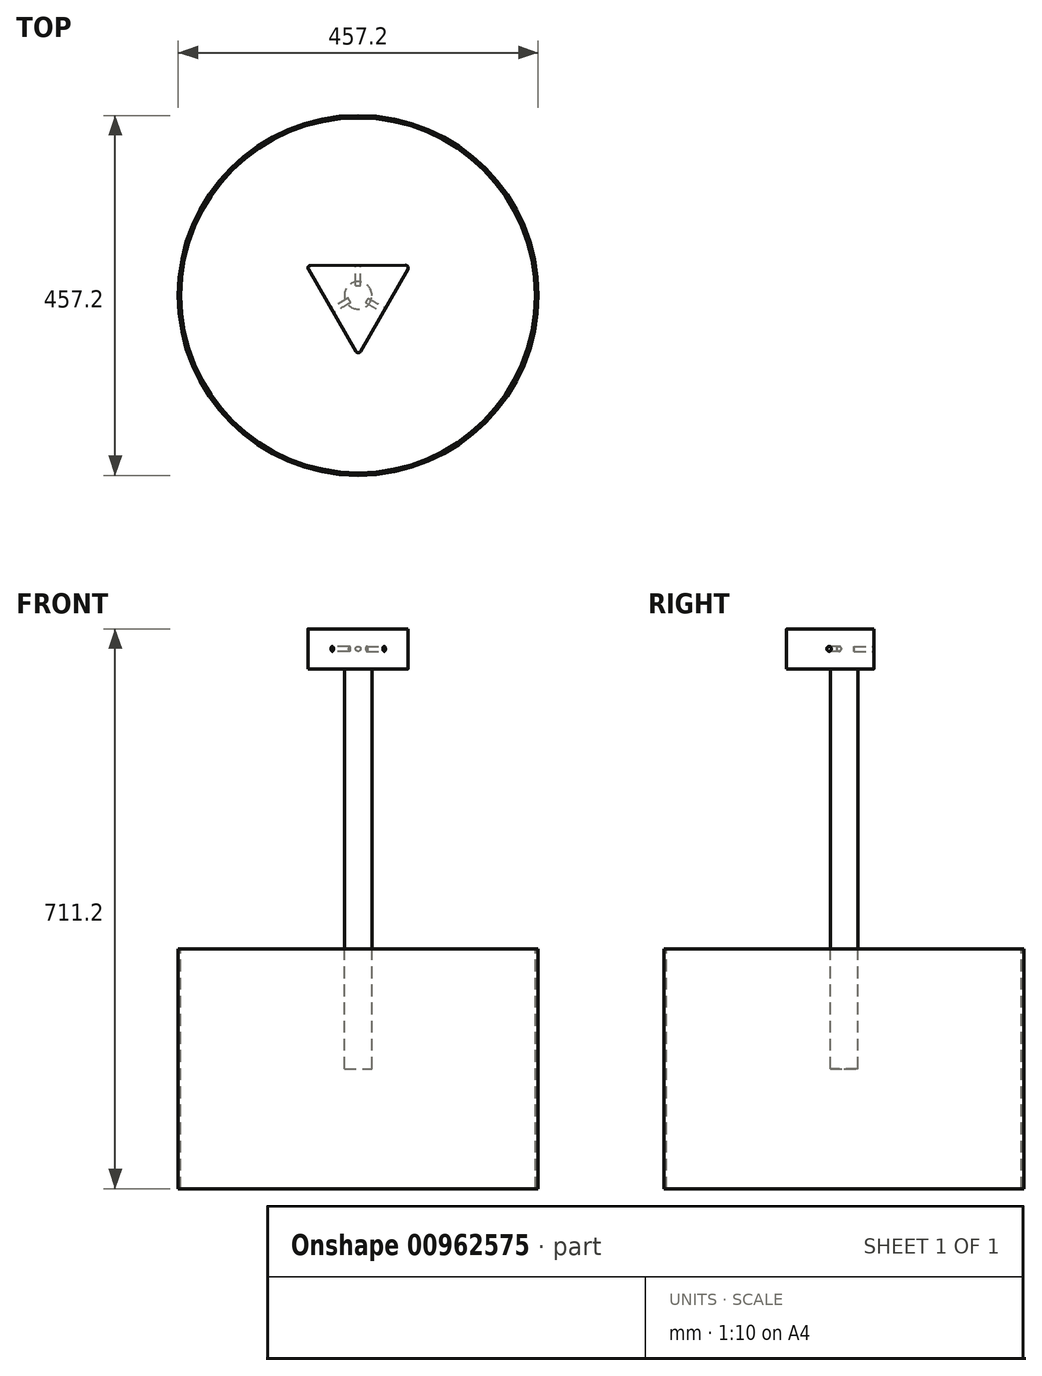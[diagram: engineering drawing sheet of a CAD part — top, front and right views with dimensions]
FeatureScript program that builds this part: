
annotation { "Feature Type Name" : "Feature", "Feature Type Description" : "" }
export const myFeature = defineFeature(function(context is Context, id is Id, definition is map)
    precondition{}
    {
        {
            var Q0;
            Q0=qCreatedBy(makeId("Top.planeOp"),FACE);
            var sketch = newSketch(context, id + "F0", { "sketchPlane" : qUnion([Q0])});
            skCircle(sketch, "E0.cCircle", {"center": v(0, 0) * mm, "radius": 38.1 * mm, "construction": true});
            skLineSegment(sketch, "E0.0", {"start": v(65.93, 38.2) * mm, "end": v(0.12, -76.2) * mm});
            skLineSegment(sketch, "E0.1", {"start": v(0.12, -76.2) * mm, "end": v(-66.05, 38) * mm});
            skLineSegment(sketch, "E0.2", {"start": v(-66.05, 38) * mm, "end": v(65.93, 38.2) * mm});
            skPoint(sketch, "E0.0.midPoint", {"position": v(33.03, -19) * mm});
            skSolve(sketch);
        }
        {
            var Q0;
            Q0=makeQuery(id+"F0.imprint","IMPRINT",FACE,{"disambiguationData":[TD([[makeQuery(id+"F0.imprint","IMPRINT",EDGE,{"derivedFrom":sQuery(id+"F0.wireOp",EDGE,"E0.0")}),-1.0]])]});
            extrude(context, id + "F1", {"entities" : qUnion([Q0]), "depth" : 50.8 * mm, "offsetDistance" : 25.4 * mm});
        }
        {
            var Q0;
            Q0=makeQuery(id+"F1.opExtrude","SWEPT_FACE",FACE,{"disambiguationData":[OSD([sQuery(id+"F0.wireOp",EDGE,"E0.0")])]});
            var sketch = newSketch(context, id + "F2", { "sketchPlane" : qUnion([Q0])});
            skCircle(sketch, "E1", {"center": v(0, 25.4) * mm, "radius": 3.18 * mm});
            skLineSegment(sketch, "E2", {"start": v(0, 50.8) * mm, "end": v(0, 0) * mm, "construction": true});
            skLineSegment(sketch, "E3", {"start": v(-66, 25.4) * mm, "end": v(66, 25.4) * mm, "construction": true});
            skSolve(sketch);
        }
        {
            var Q0;
            Q0 = qSketchRegion(id + "F2", true);
            extrude(context, id + "F3", {"entities" : qUnion([Q0]), "operationType" : NewBodyOperationType.REMOVE, "oppositeDirection" : true, "depth" : 25.4 * mm, "offsetDistance" : 25.4 * mm});
        }
        {
            var Q0;
            Q0=makeQuery(id+"F1.opExtrude","SWEPT_FACE",FACE,{"disambiguationData":[OSD([sQuery(id+"F0.wireOp",EDGE,"E0.2")])]});
            var sketch = newSketch(context, id + "F4", { "sketchPlane" : qUnion([Q0])});
            skCircle(sketch, "E4", {"center": v(0, 25.4) * mm, "radius": 3.18 * mm});
            skLineSegment(sketch, "E5", {"start": v(0, 50.8) * mm, "end": v(0, 0) * mm, "construction": true});
            skLineSegment(sketch, "E6", {"start": v(-66, 25.4) * mm, "end": v(66, 25.4) * mm, "construction": true});
            skSolve(sketch);
        }
        {
            var Q0;
            Q0=makeQuery(id+"F1.opExtrude","SWEPT_FACE",FACE,{"disambiguationData":[OSD([sQuery(id+"F0.wireOp",EDGE,"E0.1")])]});
            var sketch = newSketch(context, id + "F5", { "sketchPlane" : qUnion([Q0])});
            skCircle(sketch, "E7", {"center": v(0, 25.4) * mm, "radius": 3.18 * mm});
            skLineSegment(sketch, "E8", {"start": v(0, 50.8) * mm, "end": v(0, 0) * mm, "construction": true});
            skLineSegment(sketch, "E9", {"start": v(-66, 25.4) * mm, "end": v(66, 25.4) * mm, "construction": true});
            skSolve(sketch);
        }
        {
            var Q0;
            Q0=makeQuery(id+"F5.imprint","IMPRINT",FACE,{"disambiguationData":[TD([[makeQuery(id+"F5.imprint","IMPRINT",EDGE,{"derivedFrom":sQuery(id+"F5.wireOp",EDGE,"E7")}),1.0]])]});
            extrude(context, id + "F6", {"entities" : qUnion([Q0]), "operationType" : NewBodyOperationType.REMOVE, "oppositeDirection" : true, "depth" : 25.4 * mm, "offsetDistance" : 25.4 * mm});
        }
        {
            var Q0;
            Q0=makeQuery(id+"F4.imprint","IMPRINT",FACE,{"disambiguationData":[TD([[makeQuery(id+"F4.imprint","IMPRINT",EDGE,{"derivedFrom":sQuery(id+"F4.wireOp",EDGE,"E4")}),1.0]])]});
            extrude(context, id + "F7", {"entities" : qUnion([Q0]), "operationType" : NewBodyOperationType.REMOVE, "oppositeDirection" : true, "depth" : 25.4 * mm, "offsetDistance" : 25.4 * mm});
        }
        {
            var Q0;
            Q0=makeQuery(id+"F1.opExtrude","CAP_FACE",FACE,{"disambiguationData":[OSD([sQuery(id+"F0.wireOp",EDGE,"E0.0"),sQuery(id+"F0.wireOp",EDGE,"E0.1"),sQuery(id+"F0.wireOp",EDGE,"E0.2")])],"isStart":true});
            var sketch = newSketch(context, id + "F8", { "sketchPlane" : qUnion([Q0])});
            skCircle(sketch, "E10", {"center": v(0, 0) * mm, "radius": 17.46 * mm});
            skSolve(sketch);
        }
        {
            var Q0;
            Q0=makeQuery(id+"F8.imprint","IMPRINT",FACE,{"disambiguationData":[TD([[makeQuery(id+"F8.imprint","IMPRINT",EDGE,{"derivedFrom":sQuery(id+"F8.wireOp",EDGE,"E10")}),1.0]])]});
            extrude(context, id + "F9", {"entities" : qUnion([Q0]), "operationType" : NewBodyOperationType.ADD, "depth" : 508 * mm, "offsetDistance" : 25.4 * mm});
        }
        {
            var Q0;
            Q0=makeQuery(id+"F9.opExtrude","CAP_FACE",FACE,{"disambiguationData":[OSD([sQuery(id+"F8.wireOp",EDGE,"E10")])],"isStart":false});
            var sketch = newSketch(context, id + "F10", { "sketchPlane" : qUnion([Q0])});
            skCircle(sketch, "E11", {"center": v(0, 0) * mm, "radius": 228.6 * mm});
            skCircle(sketch, "E12", {"center": v(0, 0) * mm, "radius": 225.43 * mm});
            skSolve(sketch);
        }
        {
            var Q0;
            Q0=makeQuery(id+"F10.imprint","IMPRINT",FACE,{"disambiguationData":[TD([[makeQuery(id+"F10.imprint","IMPRINT",EDGE,{"derivedFrom":sQuery(id+"F10.wireOp",EDGE,"E11")}),1.0]])]});
            extrude(context, id + "F11", {"entities" : qUnion([Q0]), "endBound" : BoundingType.SYMMETRIC, "depth" : 304.8 * mm, "offsetDistance" : 25.4 * mm});
        }
        {
            var Q0;
            Q0=makeQuery(id+"F1.opExtrude","SWEPT_EDGE",EDGE,{"disambiguationData":[OSD([sQuery(id+"F0.wireOp",EDGE,"E0.0"),sQuery(id+"F0.wireOp",EDGE,"E0.2")])]});
            var Q1;
            Q1=makeQuery(id+"F1.opExtrude","SWEPT_EDGE",EDGE,{"disambiguationData":[OSD([sQuery(id+"F0.wireOp",EDGE,"E0.0"),sQuery(id+"F0.wireOp",EDGE,"E0.1")])]});
            var Q2;
            Q2=makeQuery(id+"F1.opExtrude","SWEPT_EDGE",EDGE,{"disambiguationData":[OSD([sQuery(id+"F0.wireOp",EDGE,"E0.1"),sQuery(id+"F0.wireOp",EDGE,"E0.2")])]});
            fillet(context, id + "F12", {"entities" : qUnion([Q0, Q1, Q2]), "radius" : 3.17 * mm, "tangentPropagation" : true, "allowEdgeOverflow" : false});
        }
    });
